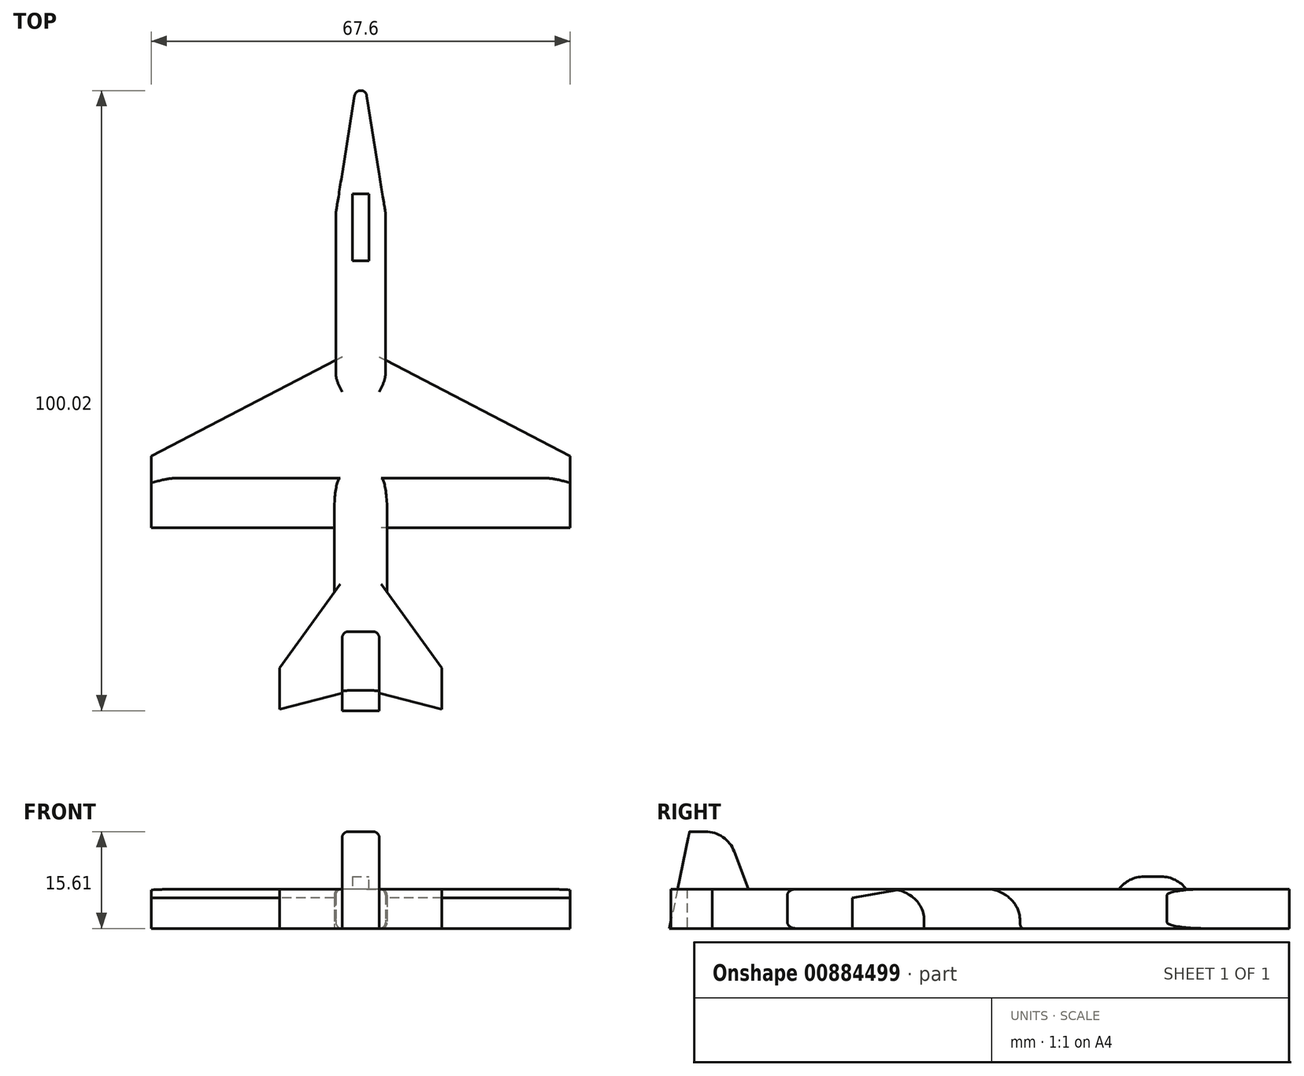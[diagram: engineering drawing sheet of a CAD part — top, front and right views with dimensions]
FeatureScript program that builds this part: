
annotation { "Feature Type Name" : "Feature", "Feature Type Description" : "" }
export const myFeature = defineFeature(function(context is Context, id is Id, definition is map)
    precondition{}
    {
        {
            var Q0;
            Q0=qCreatedBy(makeId("Top.planeOp"),FACE);
            var sketch = newSketch(context, id + "F0", { "sketchPlane" : qUnion([Q0])});
            skLineSegment(sketch, "E0", {"start": v(0, 35.73) * mm, "end": v(-4, 10.62) * mm});
            skLineSegment(sketch, "E1", {"start": v(-4, 10.62) * mm, "end": v(-4, -13.1) * mm});
            skLineSegment(sketch, "E2", {"start": v(-4, -13.1) * mm, "end": v(-33.8, -28.56) * mm});
            skLineSegment(sketch, "E3", {"start": v(-33.8, -28.56) * mm, "end": v(-33.8, -40.14) * mm});
            skLineSegment(sketch, "E4", {"start": v(-33.8, -40.14) * mm, "end": v(-4.28, -40.14) * mm});
            skLineSegment(sketch, "E5", {"start": v(-4.28, -40.14) * mm, "end": v(-4.28, -50.63) * mm});
            skLineSegment(sketch, "E6", {"start": v(-4.28, -50.63) * mm, "end": v(-13.1, -62.77) * mm});
            skLineSegment(sketch, "E7", {"start": v(-13.1, -62.77) * mm, "end": v(-13.1, -69.39) * mm});
            skLineSegment(sketch, "E8", {"start": v(-13.1, -69.39) * mm, "end": v(0, -66.08) * mm});
            skLineSegment(sketch, "E9", {"start": v(0, -66.08) * mm, "end": v(0, 35.73) * mm});
            skSolve(sketch);
        }
        {
            var Q0;
            Q0=qSketchRegion(id+"F0",true);
            extrude(context, id + "F1", {"entities" : qUnion([Q0]), "depth" : 6.35 * mm, "offsetDistance" : 25.4 * mm});
        }
        {
            var Q0;
            Q0=makeQuery(id+"F1.opExtrude","CAP_FACE",FACE,{"disambiguationData":[OSD([sQuery(id+"F0.wireOp",EDGE,"E0"),sQuery(id+"F0.wireOp",EDGE,"E1"),sQuery(id+"F0.wireOp",EDGE,"E2"),sQuery(id+"F0.wireOp",EDGE,"E3"),sQuery(id+"F0.wireOp",EDGE,"E4"),sQuery(id+"F0.wireOp",EDGE,"E5"),sQuery(id+"F0.wireOp",EDGE,"E6"),sQuery(id+"F0.wireOp",EDGE,"E7"),sQuery(id+"F0.wireOp",EDGE,"E8"),sQuery(id+"F0.wireOp",EDGE,"E9")])],"isStart":false});
            var sketch = newSketch(context, id + "F2", { "sketchPlane" : qUnion([Q0])});
            skLineSegment(sketch, "E10.bottom", {"start": v(0, 13.73) * mm, "end": v(-1.35, 13.73) * mm});
            skLineSegment(sketch, "E10.top", {"start": v(0, 2.88) * mm, "end": v(-1.35, 2.88) * mm});
            skLineSegment(sketch, "E10.left", {"start": v(0, 13.73) * mm, "end": v(0, 2.88) * mm});
            skLineSegment(sketch, "E10.right", {"start": v(-1.35, 13.73) * mm, "end": v(-1.35, 2.88) * mm});
            skSolve(sketch);
        }
        {
            var Q0;
            Q0=qSketchRegion(id+"F2",true);
            extrude(context, id + "F3", {"entities" : qUnion([Q0]), "operationType" : NewBodyOperationType.ADD, "depth" : 2 * mm, "offsetDistance" : 25 * mm});
        }
        {
            var Q0;
            Q0=qCreatedBy(makeId("Right.planeOp"),FACE);
            var sketch = newSketch(context, id + "F4", { "sketchPlane" : qUnion([Q0])});
            skLineSegment(sketch, "E11", {"start": v(-54.45, 0) * mm, "end": v(-59.2, 12.4) * mm});
            skLineSegment(sketch, "E12", {"start": v(-63.86, 15.61) * mm, "end": v(-66.4, 15.61) * mm});
            skLineSegment(sketch, "E13", {"start": v(-66.4, 15.61) * mm, "end": v(-69.65, 0) * mm});
            skLineSegment(sketch, "E14", {"start": v(-69.65, 0) * mm, "end": v(-54.45, 0) * mm});
            skPoint(sketch, "E15.visualSharp", {"position": v(-60.42, 15.61) * mm});
            skArc(sketch, "E15.filletArc", {"start": v(-59.2, 12.4) * mm, "mid": v(-61.03, 14.73) * mm, "end": v(-63.86, 15.61) * mm});
            skSolve(sketch);
        }
        {
            var Q0;
            Q0=qSketchRegion(id+"F4",true);
            extrude(context, id + "F5", {"entities" : qUnion([Q0]), "operationType" : NewBodyOperationType.ADD, "depth" : -3 * mm, "offsetDistance" : 25 * mm});
        }
        {
            var Q0;
            Q0=makeQuery(id+"F1.opExtrude","SWEPT_BODY",BODY,{"disambiguationData":[OSD([sQuery(id+"F0.wireOp",EDGE,"E0"),sQuery(id+"F0.wireOp",EDGE,"E1"),sQuery(id+"F0.wireOp",EDGE,"E2"),sQuery(id+"F0.wireOp",EDGE,"E3"),sQuery(id+"F0.wireOp",EDGE,"E4"),sQuery(id+"F0.wireOp",EDGE,"E5"),sQuery(id+"F0.wireOp",EDGE,"E6"),sQuery(id+"F0.wireOp",EDGE,"E7"),sQuery(id+"F0.wireOp",EDGE,"E8"),sQuery(id+"F0.wireOp",EDGE,"E9")])]});
            var Q1;
            Q1=makeQuery(id+"F5.boolean.opBoolean","MERGE",FACE,{"derivedFrom":[makeQuery(id+"F3.boolean.opBoolean","MERGE",FACE,{"derivedFrom":[makeQuery(id+"F1.opExtrude","SWEPT_FACE",FACE,{"disambiguationData":[OSD([sQuery(id+"F0.wireOp",EDGE,"E9")])]}),makeQuery(id+"F3.opExtrude","SWEPT_FACE",FACE,{"disambiguationData":[OSD([sQuery(id+"F2.wireOp",EDGE,"E10.left")])]})]}),makeQuery(id+"F5.opExtrude","CAP_FACE",FACE,{"disambiguationData":[OSD([sQuery(id+"F4.wireOp",EDGE,"E11"),sQuery(id+"F4.wireOp",EDGE,"E12"),sQuery(id+"F4.wireOp",EDGE,"E13"),sQuery(id+"F4.wireOp",EDGE,"E14"),sQuery(id+"F4.wireOp",EDGE,"E15.filletArc")])],"isStart":true})]});
            mirror(context, id + "F6", {"operationType" : NewBodyOperationType.ADD, "entities" : qUnion([Q0]), "mirrorPlane" : qUnion([Q1])});
        }
        {
            var Q0;
            Q0=makeQuery(id+"F1.opExtrude","CAP_EDGE",EDGE,{"disambiguationData":[OSD([sQuery(id+"F0.wireOp",EDGE,"E2")])],"isStart":false});
            var Q1;
            Q1=makeQuery(id+"F6.opPattern","COPY",EDGE,{"derivedFrom":makeQuery(id+"F1.opExtrude","CAP_EDGE",EDGE,{"disambiguationData":[OSD([sQuery(id+"F0.wireOp",EDGE,"E2")])],"isStart":false}),"instanceName":"1"});
            fillet(context, id + "F7", {"entities" : qUnion([Q0, Q1]), "radius" : 5 * mm, "tangentPropagation" : true, "allowEdgeOverflow" : false});
        }
        {
            var Q0;
            {var subQ0=makeQuery(id+"F3.opExtrude","CAP_EDGE",EDGE,{"disambiguationData":[OSD([sQuery(id+"F2.wireOp",EDGE,"E10.bottom")])],"isStart":false});Q0=makeQuery(id+"F6.boolean.opBoolean","MERGE",EDGE,{"derivedFrom":[subQ0,makeQuery(id+"F6.opPattern","COPY",EDGE,{"derivedFrom":subQ0,"instanceName":"1"})]});}
            fillet(context, id + "F8", {"entities" : qUnion([Q0]), "radius" : 5 * mm, "tangentPropagation" : true, "allowEdgeOverflow" : false});
        }
        {
            var Q0;
            {var subQ0=makeQuery(id+"F3.opExtrude","CAP_EDGE",EDGE,{"disambiguationData":[OSD([sQuery(id+"F2.wireOp",EDGE,"E10.top")])],"isStart":false});Q0=makeQuery(id+"F6.boolean.opBoolean","MERGE",EDGE,{"derivedFrom":[subQ0,makeQuery(id+"F6.opPattern","COPY",EDGE,{"derivedFrom":subQ0,"instanceName":"1"})]});}
            fillet(context, id + "F9", {"entities" : qUnion([Q0]), "radius" : 5 * mm, "tangentPropagation" : true, "allowEdgeOverflow" : false});
        }
        {
            var Q0;
            {var subQ0=makeQuery(id+"F1.opExtrude","SWEPT_EDGE",EDGE,{"disambiguationData":[OSD([sQuery(id+"F0.wireOp",EDGE,"E0"),sQuery(id+"F0.wireOp",EDGE,"E9")])]});Q0=makeQuery(id+"F6.boolean.opBoolean","MERGE",EDGE,{"derivedFrom":[subQ0,makeQuery(id+"F6.opPattern","COPY",EDGE,{"derivedFrom":subQ0,"instanceName":"1"})]});}
            fillet(context, id + "F10", {"entities" : qUnion([Q0]), "radius" : 1 * mm, "tangentPropagation" : true, "allowEdgeOverflow" : false});
        }
        {
            var Q0;
            Q0=makeQuery(id+"F1.opExtrude","CAP_EDGE",EDGE,{"disambiguationData":[OSD([sQuery(id+"F0.wireOp",EDGE,"E4")])],"isStart":false});
            var Q1;
            Q1=makeQuery(id+"F6.opPattern","COPY",EDGE,{"derivedFrom":makeQuery(id+"F1.opExtrude","CAP_EDGE",EDGE,{"disambiguationData":[OSD([sQuery(id+"F0.wireOp",EDGE,"E4")])],"isStart":false}),"instanceName":"1"});
            chamfer(context, id + "F11", {"entities" : qUnion([Q0, Q1]), "chamferType" : ChamferType.OFFSET_ANGLE, "width" : 8 * mm, "oppositeDirection" : false, "angle" : 10 * degree, "tangentPropagation" : true});
        }
        {
            var Q0;
            Q0=makeQuery(id+"F5.opExtrude","CAP_EDGE",EDGE,{"disambiguationData":[OSD([sQuery(id+"F4.wireOp",EDGE,"E11")])],"isStart":false});
            fillet(context, id + "F12", {"entities" : qUnion([Q0]), "radius" : 1 * mm, "tangentPropagation" : true, "allowEdgeOverflow" : false});
        }
        {
            var Q0;
            Q0=makeQuery(id+"F6.opPattern","COPY",EDGE,{"derivedFrom":makeQuery(id+"F5.opExtrude","CAP_EDGE",EDGE,{"disambiguationData":[OSD([sQuery(id+"F4.wireOp",EDGE,"E11")])],"isStart":false}),"instanceName":"1"});
            fillet(context, id + "F13", {"entities" : qUnion([Q0]), "radius" : 1 * mm, "tangentPropagation" : true, "allowEdgeOverflow" : false});
        }
        {
            var Q0;
            Q0=makeQuery(id+"F6.opPattern","COPY",EDGE,{"derivedFrom":makeQuery(id+"F1.opExtrude","CAP_EDGE",EDGE,{"disambiguationData":[OSD([sQuery(id+"F0.wireOp",EDGE,"E1")])],"isStart":false}),"instanceName":"1"});
            var Q1;
            Q1=makeQuery(id+"F1.opExtrude","CAP_EDGE",EDGE,{"disambiguationData":[OSD([sQuery(id+"F0.wireOp",EDGE,"E1")])],"isStart":false});
            var Q2;
            Q2=makeQuery(id+"F1.opExtrude","CAP_EDGE",EDGE,{"disambiguationData":[OSD([sQuery(id+"F0.wireOp",EDGE,"E5")])],"isStart":false});
            var Q3;
            Q3=makeQuery(id+"F6.opPattern","COPY",EDGE,{"derivedFrom":makeQuery(id+"F1.opExtrude","CAP_EDGE",EDGE,{"disambiguationData":[OSD([sQuery(id+"F0.wireOp",EDGE,"E5")])],"isStart":false}),"instanceName":"1"});
            fillet(context, id + "F14", {"entities" : qUnion([Q0, Q1, Q2, Q3]), "radius" : 1 * mm, "tangentPropagation" : true, "allowEdgeOverflow" : false});
        }
        {
            var Q0;
            Q0=makeQuery(id+"F6.opPattern","COPY",EDGE,{"derivedFrom":makeQuery(id+"F1.opExtrude","CAP_EDGE",EDGE,{"disambiguationData":[OSD([sQuery(id+"F0.wireOp",EDGE,"E1")])],"isStart":true}),"instanceName":"1"});
            var Q1;
            Q1=makeQuery(id+"F1.opExtrude","CAP_EDGE",EDGE,{"disambiguationData":[OSD([sQuery(id+"F0.wireOp",EDGE,"E1")])],"isStart":true});
            var Q2;
            Q2=makeQuery(id+"F6.opPattern","COPY",EDGE,{"derivedFrom":makeQuery(id+"F1.opExtrude","CAP_EDGE",EDGE,{"disambiguationData":[OSD([sQuery(id+"F0.wireOp",EDGE,"E5")])],"isStart":true}),"instanceName":"1"});
            fillet(context, id + "F15", {"entities" : qUnion([Q0, Q1, Q2]), "radius" : 1 * mm, "tangentPropagation" : true, "allowEdgeOverflow" : false});
        }
    });
